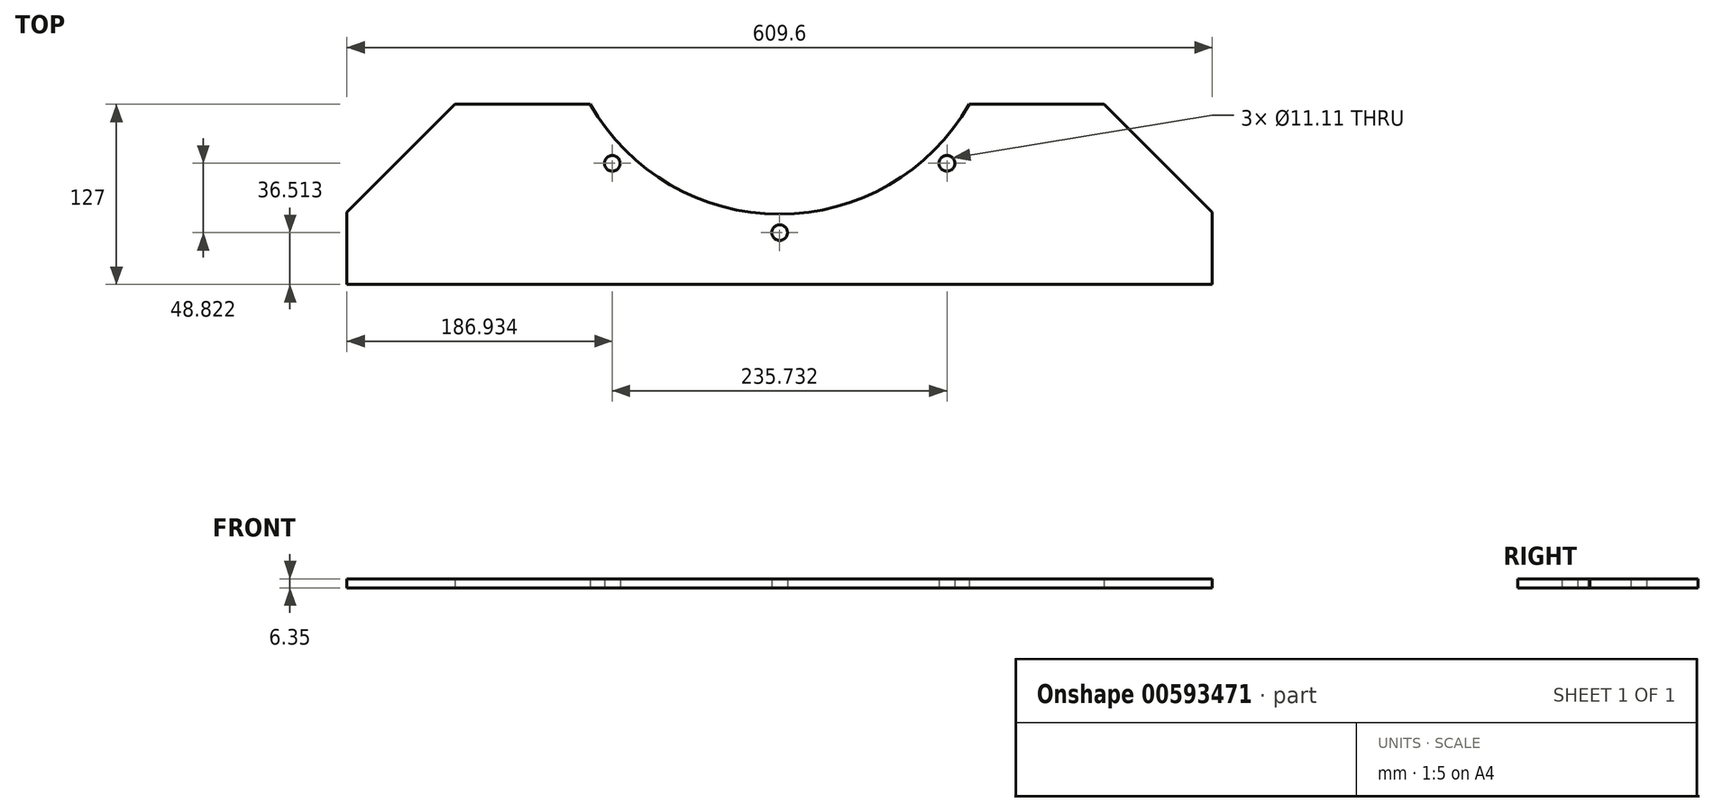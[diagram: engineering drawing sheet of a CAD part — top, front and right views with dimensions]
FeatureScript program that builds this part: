
annotation { "Feature Type Name" : "Feature", "Feature Type Description" : "" }
export const myFeature = defineFeature(function(context is Context, id is Id, definition is map)
    precondition{}
    {
        {
            var Q0;
            Q0=qCreatedBy(makeId("Top.planeOp"),FACE);
            var sketch = newSketch(context, id + "F0", { "sketchPlane" : qUnion([Q0])});
            skLineSegment(sketch, "E0.bottom", {"start": v(0, 0) * mm, "end": v(609.6, 0) * mm});
            skLineSegment(sketch, "E0.top", {"start": v(76.2, 127) * mm, "end": v(171.35, 127) * mm});
            skLineSegment(sketch, "E0.left", {"start": v(0, 0) * mm, "end": v(0, 50.8) * mm});
            skLineSegment(sketch, "E0.right", {"start": v(609.6, 0) * mm, "end": v(609.6, 50.8) * mm});
            skArc(sketch, "E1", {"start": v(171.35, 127) * mm, "mid": v(304.8, 49.53) * mm, "end": v(438.25, 127) * mm});
            skPoint(sketch, "E1.centerSnap0", {"position": v(304.8, 127) * mm});
            skLineSegment(sketch, "E2.trimOffspring", {"start": v(438.25, 127) * mm, "end": v(533.4, 127) * mm});
            skLineSegment(sketch, "E3", {"start": v(0, 50.8) * mm, "end": v(76.2, 127) * mm});
            skPoint(sketch, "E4.orphan", {"position": v(0, 127) * mm});
            skLineSegment(sketch, "E5", {"start": v(533.4, 127) * mm, "end": v(609.6, 50.8) * mm});
            skPoint(sketch, "E6.orphan", {"position": v(609.6, 127) * mm});
            skCircle(sketch, "E7", {"center": v(304.8, 203.2) * mm, "radius": 166.69 * mm, "construction": true});
            skCircle(sketch, "E8", {"center": v(304.8, 36.51) * mm, "radius": 5.56 * mm});
            skCircle(sketch, "E9.1.0", {"center": v(186.93, 85.33) * mm, "radius": 5.56 * mm});
            skLineSegment(sketch, "E9.anchor1", {"start": v(304.8, 203.2) * mm, "end": v(304.8, 36.51) * mm, "construction": true});
            skLineSegment(sketch, "E9.anchor2", {"start": v(304.8, 203.2) * mm, "end": v(186.93, 85.33) * mm, "construction": true});
            skCircle(sketch, "E10.1.0", {"center": v(422.67, 85.33) * mm, "radius": 5.56 * mm});
            skLineSegment(sketch, "E10.anchor2", {"start": v(304.8, 203.2) * mm, "end": v(422.67, 85.33) * mm, "construction": true});
            skSolve(sketch);
        }
        {
            var Q0;
            Q0=makeQuery(id+"F0.imprint","IMPRINT",FACE,{"disambiguationData":[TD([[makeQuery(id+"F0.imprint","IMPRINT",EDGE,{"derivedFrom":sQuery(id+"F0.wireOp",EDGE,"E0.bottom")}),1.0]])]});
            extrude(context, id + "F1", {"entities" : qUnion([Q0]), "depth" : 6.35 * mm, "offsetDistance" : 25.4 * mm});
        }
    });
